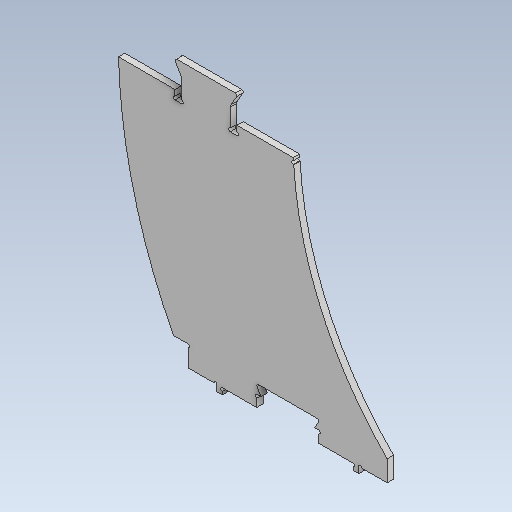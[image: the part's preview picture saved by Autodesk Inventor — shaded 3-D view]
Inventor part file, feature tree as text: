
AUTODESK INVENTOR PART (.ipt)
format: ipt  version: 2020 (Build 240168000, 168)  size: 311,296 bytes
history: native  units: mm
features: extrude x1, sketch x1
ambient origin geometry x8: Origin, YZ Plane, XZ Plane, XY Plane, X Axis, Y Axis, Z Axis, Center Point
bodies: Body1 (feature_tree)
feature tree (2):
  extrude  "Extrusion2"  Depth=3.5mm
  sketch  "Sketch1"  dims[d13=550.0mm d17=200.0mm d18=0.0mm d19=150.0mm d54=220.0mm d56=220.0mm d57=30.0mm d59=30.0mm d73=236.680872mm d74=236.680872mm d75=576.435mm d76=472.393783mm d77=472.393783mm d78=30.0mm d81=220.0mm d82=252.393783mm d85=356.435mm d88=3.5mm d89=30.0mm d90=22.0mm d91=3.5mm d103=3.75mm d104=3.75mm d105=2.666667mm d106=30.0mm d107=20.0mm d108=2.666667mm d109=1.333333mm d110=7.333333mm d111=7.333333mm d112=7.5mm d113=3.75mm d114=3.75mm d134=3.5mm d135=65.0mm d136=65.0mm d137=7.333333mm d138=60.0deg d139=5.0mm d140=7.5mm d148=1.75mm d151=40.0mm d152=74.50599mm d153=20.666667mm d154=3.5mm d155=189.01198mm d159=1.75mm d160=1.75mm d161=1.75mm d164=7.5mm d168=21.25mm d170=30.0mm d171=1.75mm d172=10.0mm d173=3.5mm d177=3.5mm d178=65.0mm d179=65.0mm d180=7.333333mm d181=60.0deg d182=5.0mm d183=7.5mm d184=30.0mm d185=1.75mm d186=10.0mm d192=1.75mm d206=1.75mm d208=220.0mm d209=3.5mm d210=65.0mm d211=65.0mm d212=7.333333mm d213=60.0deg d214=5.0mm d215=7.5mm d216=30.0mm d217=1.75mm d218=10.0mm d219=7.0mm d220=1.75mm d222=23.0mm d226=1.75mm d228=53.623497mm d231=1.75mm d232=1.75mm d233=7.0mm d234=1.75mm d235=23.0mm d236=1.75mm d237=252.393783mm d238=7.0mm d239=0.0mm d240=3.0mm d241=3.5mm d244=3.5mm d245=0.0mm]
